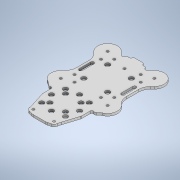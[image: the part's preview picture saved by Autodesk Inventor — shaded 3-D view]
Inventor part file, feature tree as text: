
AUTODESK INVENTOR PART (.ipt)
format: ipt  version: 2020 (Build 240168000, 168)  size: 253,440 bytes
history: native  units: mm
features: extrude x1, sketch x1
ambient origin geometry x8: Origin, YZ Plane, XZ Plane, XY Plane, X Axis, Y Axis, Z Axis, Center Point
bodies: Solid1 (feature_tree)
feature tree (2):
  extrude  "Extrusion1"  [1 undecoded]
  sketch  "Sketch1"  dims[d0=3.0mm d1=0.0mm]
note: 1 required parameter value undecoded (feature->parameter linkage not recoverable at this tier; creation-order binding heuristic only, values carry confidence <= 0.55)
